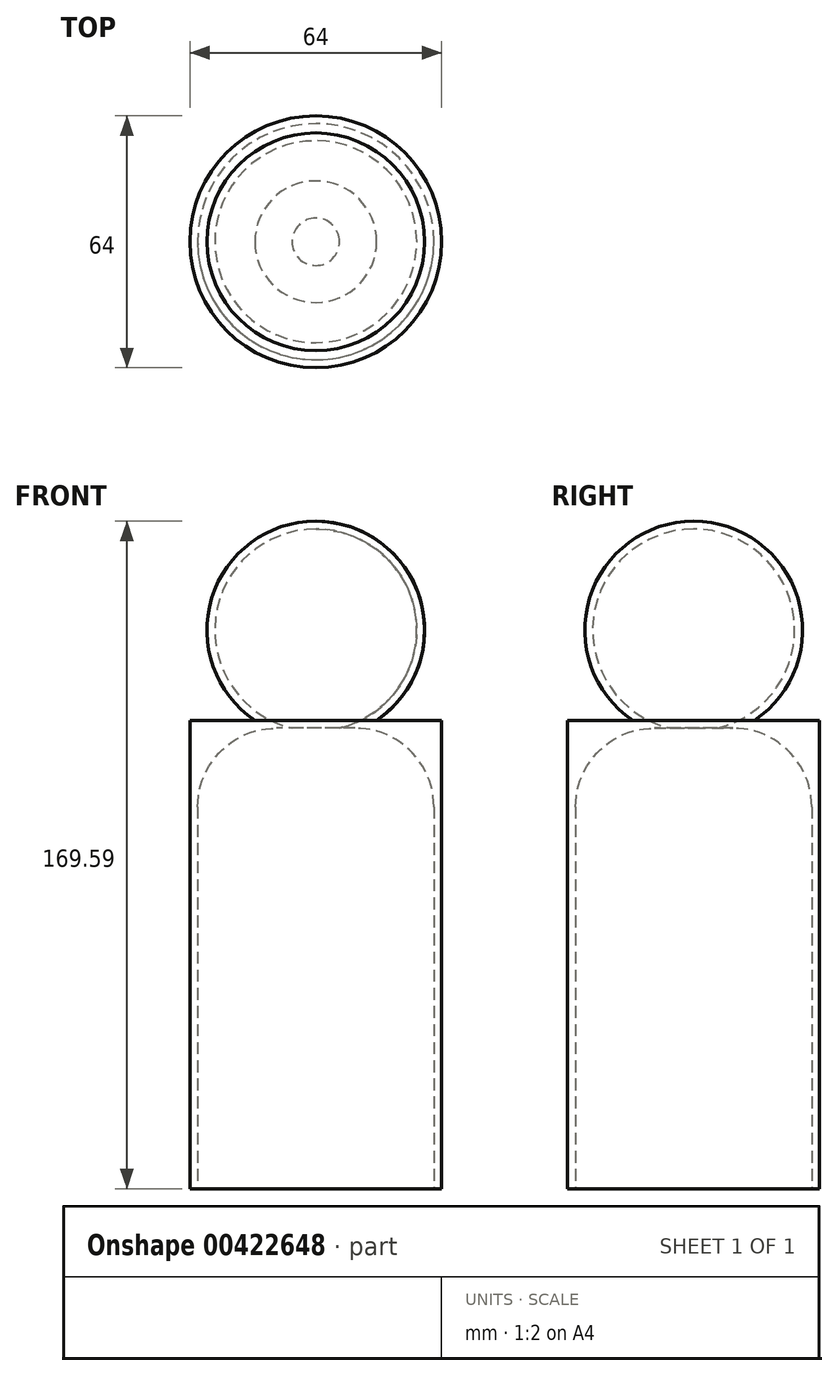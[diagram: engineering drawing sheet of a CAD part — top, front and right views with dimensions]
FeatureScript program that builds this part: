
annotation { "Feature Type Name" : "Feature", "Feature Type Description" : "" }
export const myFeature = defineFeature(function(context is Context, id is Id, definition is map)
    precondition{}
    {
        {
            var Q0;
            Q0=qCreatedBy(makeId("Front.planeOp"),FACE);
            var sketch = newSketch(context, id + "F0", { "sketchPlane" : qUnion([Q0])});
            skLineSegment(sketch, "E0", {"start": v(0, -37) * mm, "end": v(-32, -37) * mm});
            skLineSegment(sketch, "E1", {"start": v(-32, -37) * mm, "end": v(-32, 82) * mm});
            skPoint(sketch, "E2.center.orphan", {"position": v(0, 87.8) * mm});
            skLineSegment(sketch, "E3", {"start": v(-32, 82) * mm, "end": v(0, 82) * mm});
            skLineSegment(sketch, "E4", {"start": v(0, 82) * mm, "end": v(0, 74.45) * mm});
            skArc(sketch, "E5", {"start": v(0, 132.6) * mm, "mid": v(-26.45, 113.02) * mm, "end": v(-15.45, 82) * mm});
            skLineSegment(sketch, "E6", {"start": v(0, 132.6) * mm, "end": v(0, 74.45) * mm});
            skLineSegment(sketch, "E7", {"start": v(0, -37) * mm, "end": v(0, 132.6) * mm});
            skSolve(sketch);
        }
        {
            var Q0;
            Q0 = qSketchRegion(id + "F0", true);
            var Q1;
            Q1=sQuery(id+"F0.wireOp",EDGE,"E7");
            revolve(context, id + "F1", {"entities" : qUnion([Q0]), "axis" : qUnion([Q1]), "revolveType" : RevolveType.FULL});
        }
        {
            var Q0;
            Q0=makeQuery(id+"F1.opRevolve","SWEPT_FACE",FACE,{"disambiguationData":[OSD([sQuery(id+"F0.wireOp",EDGE,"E0")])]});
            shell(context, id + "F2", {"entities" : qUnion([Q0]), "thickness" : 2 * mm});
        }
        {
            var Q0;
            Q0=makeQuery(id+"F2.opShell","OFFSET_EDGE",EDGE,{"disambiguationData":[OSD([sQuery(id+"F0.wireOp",EDGE,"E1"),sQuery(id+"F0.wireOp",EDGE,"E3")])]});
            fillet(context, id + "F3", {"entities" : qUnion([Q0]), "radius" : 20 * mm, "tangentPropagation" : true, "allowEdgeOverflow" : false});
        }
    });
